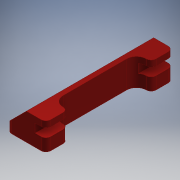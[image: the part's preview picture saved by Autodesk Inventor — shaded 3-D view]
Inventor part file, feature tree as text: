
AUTODESK INVENTOR PART (.ipt)
format: ipt  version: 2018 (Build 220112000, 112)  size: 174,592 bytes
history: native  units: mm
features: sketch x4, extrude x3, projected_geometry x2, hole x1, chamfer x1, fillet x1
ambient origin geometry x8: Origin, YZ Plane, XZ Plane, XY Plane, X Axis, Y Axis, Z Axis, Center Point
bodies: Solid1 (feature_tree)
feature tree (12):
  extrude  "Extrusion1"  Depth=26.0mm
  hole  "Hole1"  [1 undecoded]
  extrude  "Extrusion2"  Depth=2.5mm
  chamfer  "Chamfer1"  Distance=2.25mm
  extrude  "Extrusion3"  Depth=1.0mm TaperAngle=0.0deg
  fillet  "Fillet1"  Radius=2.0mm
  sketch  "Sketch1"  dims[d0=26.0mm d2=20.0mm]
  sketch  "Sketch2"  dims[d3=5.5mm d4=0.0mm d5=5.0mm]
  sketch  "Sketch3"  dims[d6=1.567mm d7=4.0mm d8=4.0mm d9=2.0mm d10=90.0deg d11=6.3mm d12=20.594885mm d13=2.5mm]
  projected_geometry  "Projected Loop1"
  sketch  "Sketch4"  dims[d14=1.8mm d15=2.25mm d16=6.0mm d17=0.0mm d18=4.0mm d19=2.0mm d20=45.0deg d21=3.0mm d22=17.0mm d23=6.0mm d24=0.0mm d25=2.0mm d26=1.0mm]
  projected_geometry  "Projected Loop2"
note: 1 required parameter value undecoded (feature->parameter linkage not recoverable at this tier; creation-order binding heuristic only, values carry confidence <= 0.55)
